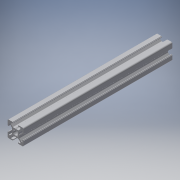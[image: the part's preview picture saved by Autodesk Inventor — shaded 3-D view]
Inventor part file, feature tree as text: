
AUTODESK INVENTOR PART (.ipt)
format: ipt  version: 2016 (Build 200138000, 138)  size: 317,952 bytes
history: native  units: in
note: dims shown in document units (in); Inventor stores cm internally (conversion verified against a paired STEP export)
features: other x3, extrude x1, sketch x1
ambient origin geometry x8: Origin, YZ Plane, XZ Plane, XY Plane, X Axis, Y Axis, Z Axis, Center Point
bodies: Solid1 (feature_tree)
feature tree (5):
  other  "Blocks"
  extrude  "Extrusion1"  [1 undecoded]
  sketch  "Sketch1"  dims[d1=0.0in]
  other  "20x20"
  other  "20x20:1"
note: 1 required parameter value undecoded (feature->parameter linkage not recoverable at this tier; creation-order binding heuristic only, values carry confidence <= 0.55)
